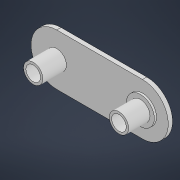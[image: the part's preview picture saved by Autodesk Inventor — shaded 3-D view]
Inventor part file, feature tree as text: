
AUTODESK INVENTOR PART (.ipt)
format: ipt  version: 2022 (Build 260153000, 153)  size: 134,144 bytes
history: native  units: in
note: dims shown in document units (in); Inventor stores cm internally (conversion verified against a paired STEP export)
features: extrude x3, sketch x3, projected_geometry x1
ambient origin geometry x8: Origin, YZ Plane, XZ Plane, XY Plane, X Axis, Y Axis, Z Axis, Center Point
bodies: Solid1 (feature_tree)
feature tree (7):
  extrude  "Extrusion1"  Depth=0.2362in
  extrude  "Extrusion2"  Depth=0.0394in TaperAngle=0.0deg
  extrude  "Extrusion3"  Depth=0.0197in
  sketch  "Sketch1"  dims[d0=0.7874in d1=0.2362in]
  sketch  "Sketch2"  dims[d2=0.1339in d3=0.0394in d4=0.0in]
  sketch  "Sketch3"  dims[d5=0.1772in d6=0.1772in d7=0.2165in d8=0.0in d9=0.2559in d10=0.0197in d11=0.0in]
  projected_geometry  "Projected Loop1"
